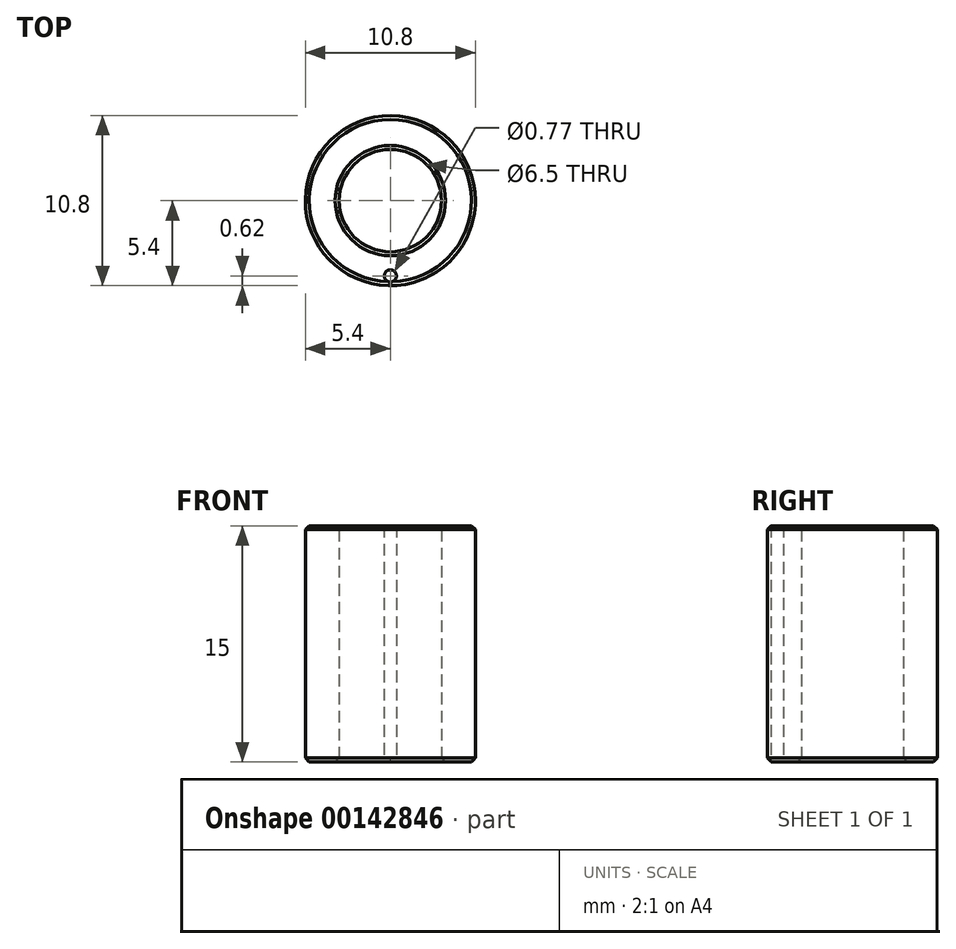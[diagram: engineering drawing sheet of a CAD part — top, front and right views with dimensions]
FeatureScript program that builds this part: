
annotation { "Feature Type Name" : "Feature", "Feature Type Description" : "" }
export const myFeature = defineFeature(function(context is Context, id is Id, definition is map)
    precondition{}
    {
        {
            var Q0;
            Q0=qCreatedBy(makeId("Top.planeOp"),FACE);
            var sketch = newSketch(context, id + "F0", { "sketchPlane" : qUnion([Q0])});
            skCircle(sketch, "E0", {"center": v(0, 0) * mm, "radius": 3.25 * mm});
            skCircle(sketch, "E1", {"center": v(0, -4.78) * mm, "radius": 0.39 * mm});
            skCircle(sketch, "E2", {"center": v(0, 0) * mm, "radius": 5.4 * mm});
            skSolve(sketch);
        }
        {
            var Q0;
            Q0 = qSketchRegion(id + "F0", true);
            extrude(context, id + "F1", {"entities" : qUnion([Q0]), "depth" : 15 * mm, "offsetDistance" : 25 * mm});
        }
        {
            var Q0;
            Q0=makeQuery(id+"F1.opExtrude","CAP_EDGE",EDGE,{"disambiguationData":[OSD([sQuery(id+"F0.wireOp",EDGE,"E0")])],"isStart":false});
            var Q1;
            Q1=makeQuery(id+"F1.opExtrude","CAP_EDGE",EDGE,{"disambiguationData":[OSD([sQuery(id+"F0.wireOp",EDGE,"E2")])],"isStart":false});
            var Q2;
            Q2=makeQuery(id+"F1.opExtrude","CAP_EDGE",EDGE,{"disambiguationData":[OSD([sQuery(id+"F0.wireOp",EDGE,"E0")])],"isStart":true});
            chamfer(context, id + "F2", {"entities" : qUnion([Q0, Q1, Q2]), "width" : .25 * mm, "tangentPropagation" : true});
        }
        {
            var Q0;
            Q0=makeQuery(id+"F1.opExtrude","CAP_EDGE",EDGE,{"disambiguationData":[OSD([sQuery(id+"F0.wireOp",EDGE,"E2")])],"isStart":true});
            chamfer(context, id + "F3", {"entities" : qUnion([Q0]), "width" : .25 * mm, "tangentPropagation" : true});
        }
    });
